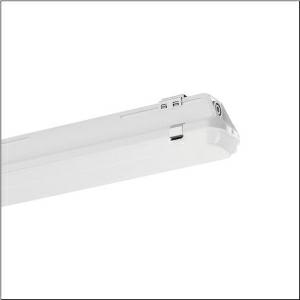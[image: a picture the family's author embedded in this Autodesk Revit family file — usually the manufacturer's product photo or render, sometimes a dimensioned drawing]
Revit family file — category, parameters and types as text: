
# Revit family: monsun_r__11_51fp20dp4b0u_a00c
name_source: partatom
category: Lighting Fixtures
units: mm (PartAtom-declared; Revit-internal decimal feet)

## family parameters
Cut with Voids When Loaded = No
Host = Face
Light Source = No
Part Type = Normal
Room Calculation Point = No
Round Connector Dimension = Use Diameter
Shared = No

## types (1)
- --- (1 x LED, 10950 lm, 63.7 W, 4000K)
    Apparent Load = 64 VA
    CIE Flux Codes = 45 75 93 94 100
    Color Rendering = 80
    Color Temperature = 4000K
    Default Elevation = 1800 mm
    Description = Monsun® 11, damp-proof luminaire, chain hanger, primary optical cover: enclosure, of PC, light emission: direct distribution, primary light characteristic: symmetric, installation type: suspended mounting, surface-mounted, horizontal mounting, vertical mounting, LED, rated luminous flux: 10.950lm, luminous efficacy: 172lm/W, light colour: 840, colour temperature: 4000K, control gear: DALI 2, with terminal, 5-pole, max. 2.5mm², mains connection: 220..240V, AC, 50/60Hz, rated input power: 64W, luminaire housing, of glass-fibre reinforced polyester, uncoated, bright grey, incl. chain hanger, length: 1.590mm, width: 90mm, height: 88mm, clip for enclosure, of stainless steel (V2A), ceiling mounting element, of stainless steel (V2A), chain hanger, of stainless steel (V2A), protection rating (complete): IP66, insulation class (complete): insulation class I (protective earthing), certification: CE, ENEC, VDE, UKCA, protection symbol: D, impact resistance: IK08, permissible operating ambient temperature: -40..+35°C, standard: EN 50419, EN 60598-2-1, contact your sales advisor before using the luminaires in applications with unclear chemical exposure, large temperature fluctuations or condensation-forming humidity, LABS conformity tested according to VDMA 24364:2018-05, no direct snow, no direct sun, no direct rain, for indoor or canopied outdoor use, corresponds to IFS (International Featured Standards) requirements for safety and quality in the food industry, packaging unit: 1 piece
    Height = 89 mm
    Lamp = 1 x LED
    Lamp Light Flux = 10950 lm
    Lamp Power = 63.7 W
    Lamp count = 1
    Length = 1590 mm
    Luminous efficacy = 172 lm/W
    Manufacturer = Siteco
    ModVariant = No
    Model = 51FP20DP4B0U
    Mounting Place = Ceiling
    Mounting Type = Surface mounted
    Number of Poles = 1
    OnlyDefault = Yes
    Power Factor = 1
    Product Name = Monsun® 11
    Product group = damp-proof luminaire
    ProductGroupID = 300
    Protection Class = Protection class I
    Protection Degree = IP 66
    RLX_Detail_Level = 1
    RLX_Emergency_Light_Flux = 0 lm
    RLX_Emergency_Type = 0
    RLX_Emergency_Type_DB = No
    RlxData = <blob elided: 92129 chars, md5=fad67850>
    Socket = socket
    Standby Power = 0 W
    System Light Flux = 10950 lm
    System Power = 64 W
    Type Comments = factory setting: luminous flux: 100 % | dim-lin: 254 | 441 mA
    Type Image = l_1349237.jpg
    URL = http://relux.com
    VarID = @adj_022990
    Voltage = 0 V
    Weight = 0.00 kg
    Width = 90 mm

## geometry (parser evidence)
native form markers: Blend x4, Sweep x12
no freeform markers — native parametric forms only
